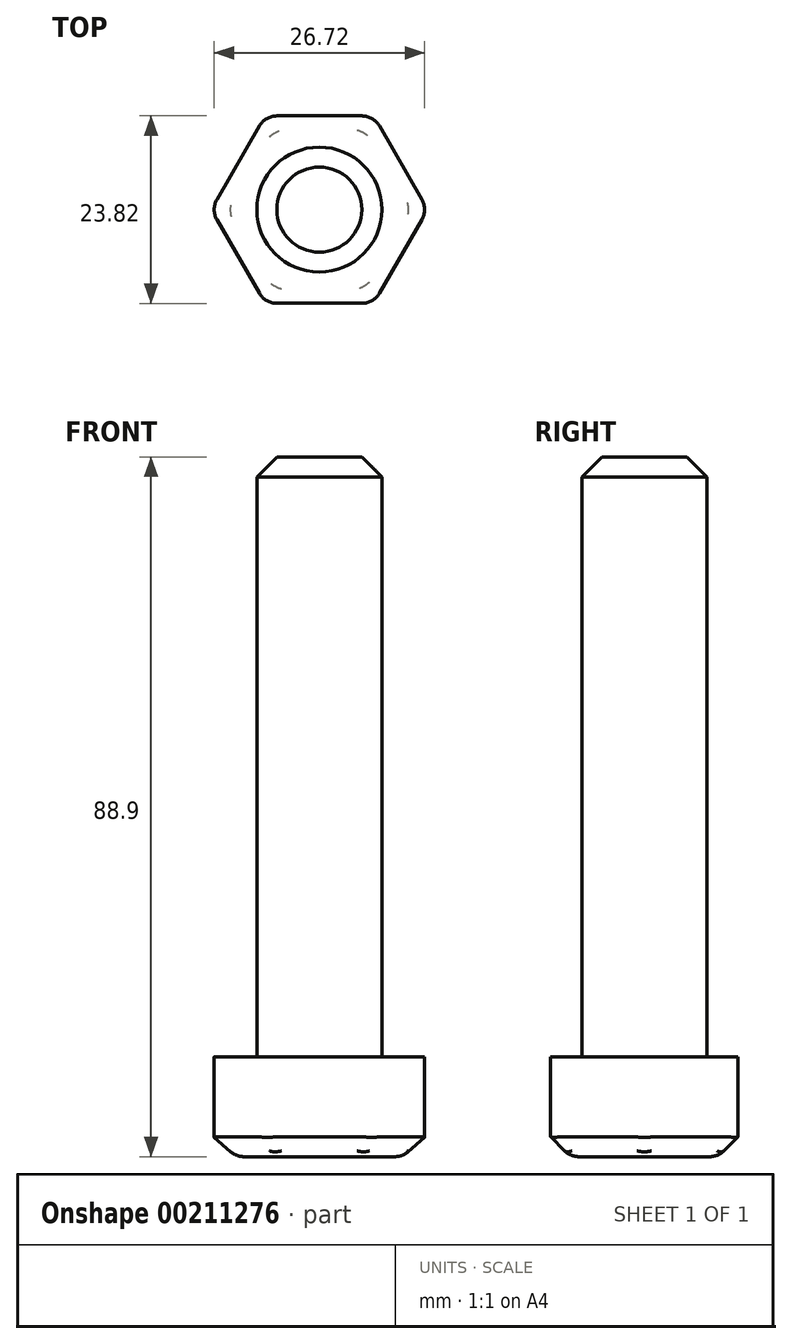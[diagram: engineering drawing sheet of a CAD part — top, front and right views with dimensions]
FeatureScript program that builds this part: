
annotation { "Feature Type Name" : "Feature", "Feature Type Description" : "" }
export const myFeature = defineFeature(function(context is Context, id is Id, definition is map)
    precondition{}
    {
        {
            var Q0;
            Q0=qCreatedBy(makeId("Top.planeOp"),FACE);
            var sketch = newSketch(context, id + "F0", { "sketchPlane" : qUnion([Q0])});
            skCircle(sketch, "E0.cCircle", {"center": v(0, 0) * mm, "radius": 11.9 * mm, "construction": true});
            skLineSegment(sketch, "E0.0", {"start": v(-6.87, 11.9) * mm, "end": v(6.87, 11.9) * mm});
            skLineSegment(sketch, "E0.1", {"start": v(6.87, 11.9) * mm, "end": v(13.75, 0) * mm});
            skLineSegment(sketch, "E0.2", {"start": v(13.75, 0) * mm, "end": v(6.87, -11.9) * mm});
            skLineSegment(sketch, "E0.3", {"start": v(6.87, -11.9) * mm, "end": v(-6.87, -11.9) * mm});
            skLineSegment(sketch, "E0.4", {"start": v(-6.87, -11.9) * mm, "end": v(-13.75, 0) * mm});
            skLineSegment(sketch, "E0.5", {"start": v(-13.75, 0) * mm, "end": v(-6.87, 11.9) * mm});
            skPoint(sketch, "E0.0.midPoint", {"position": v(0, 11.9) * mm});
            skSolve(sketch);
        }
        {
            var Q0;
            Q0=qSketchRegion(id+"F0",true);
            extrude(context, id + "F1", {"entities" : qUnion([Q0]), "depth" : 12.7 * mm});
        }
        {
            var Q0;
            Q0=makeQuery(id+"F1.opExtrude","CAP_FACE",FACE,{"disambiguationData":[OSD([sQuery(id+"F0.wireOp",EDGE,"E0.0"),sQuery(id+"F0.wireOp",EDGE,"E0.1"),sQuery(id+"F0.wireOp",EDGE,"E0.2"),sQuery(id+"F0.wireOp",EDGE,"E0.3"),sQuery(id+"F0.wireOp",EDGE,"E0.4"),sQuery(id+"F0.wireOp",EDGE,"E0.5")])],"isStart":false});
            var sketch = newSketch(context, id + "F2", { "sketchPlane" : qUnion([Q0])});
            skCircle(sketch, "E1", {"center": v(0, 0) * mm, "radius": 7.94 * mm});
            skSolve(sketch);
        }
        {
            var Q0;
            Q0=qSketchRegion(id+"F2",true);
            extrude(context, id + "F3", {"entities" : qUnion([Q0]), "operationType" : NewBodyOperationType.ADD, "depth" : 76.2 * mm});
        }
        {
            var Q0;
            Q0=makeQuery(id+"F3.opExtrude","CAP_EDGE",EDGE,{"disambiguationData":[OSD([sQuery(id+"F2.wireOp",EDGE,"E1")])],"isStart":false});
            var Q1;
            Q1=makeQuery(id+"F1.opExtrude","CAP_EDGE",EDGE,{"disambiguationData":[OSD([sQuery(id+"F0.wireOp",EDGE,"E0.5")])],"isStart":true});
            var Q2;
            Q2=makeQuery(id+"F1.opExtrude","CAP_EDGE",EDGE,{"disambiguationData":[OSD([sQuery(id+"F0.wireOp",EDGE,"E0.0")])],"isStart":true});
            var Q3;
            Q3=makeQuery(id+"F1.opExtrude","CAP_EDGE",EDGE,{"disambiguationData":[OSD([sQuery(id+"F0.wireOp",EDGE,"E0.1")])],"isStart":true});
            var Q4;
            Q4=makeQuery(id+"F1.opExtrude","CAP_EDGE",EDGE,{"disambiguationData":[OSD([sQuery(id+"F0.wireOp",EDGE,"E0.2")])],"isStart":true});
            var Q5;
            Q5=makeQuery(id+"F1.opExtrude","CAP_EDGE",EDGE,{"disambiguationData":[OSD([sQuery(id+"F0.wireOp",EDGE,"E0.3")])],"isStart":true});
            var Q6;
            Q6=makeQuery(id+"F1.opExtrude","CAP_EDGE",EDGE,{"disambiguationData":[OSD([sQuery(id+"F0.wireOp",EDGE,"E0.4")])],"isStart":true});
            chamfer(context, id + "F4", {"entities" : qUnion([Q0, Q1, Q2, Q3, Q4, Q5, Q6]), "width" : 2.54 * mm, "tangentPropagation" : true});
        }
        {
            var Q0;
            Q0=makeQuery(id+"F1.opExtrude","SWEPT_EDGE",EDGE,{"disambiguationData":[OSD([sQuery(id+"F0.wireOp",EDGE,"E0.0"),sQuery(id+"F0.wireOp",EDGE,"E0.5")])]});
            var Q1;
            Q1=makeQuery(id+"F1.opExtrude","SWEPT_EDGE",EDGE,{"disambiguationData":[OSD([sQuery(id+"F0.wireOp",EDGE,"E0.0"),sQuery(id+"F0.wireOp",EDGE,"E0.1")])]});
            var Q2;
            Q2=makeQuery(id+"F1.opExtrude","SWEPT_EDGE",EDGE,{"disambiguationData":[OSD([sQuery(id+"F0.wireOp",EDGE,"E0.1"),sQuery(id+"F0.wireOp",EDGE,"E0.2")])]});
            var Q3;
            Q3=makeQuery(id+"F1.opExtrude","SWEPT_EDGE",EDGE,{"disambiguationData":[OSD([sQuery(id+"F0.wireOp",EDGE,"E0.2"),sQuery(id+"F0.wireOp",EDGE,"E0.3")])]});
            var Q4;
            Q4=makeQuery(id+"F1.opExtrude","SWEPT_EDGE",EDGE,{"disambiguationData":[OSD([sQuery(id+"F0.wireOp",EDGE,"E0.3"),sQuery(id+"F0.wireOp",EDGE,"E0.4")])]});
            var Q5;
            Q5=makeQuery(id+"F1.opExtrude","SWEPT_EDGE",EDGE,{"disambiguationData":[OSD([sQuery(id+"F0.wireOp",EDGE,"E0.4"),sQuery(id+"F0.wireOp",EDGE,"E0.5")])]});
            var Q6;
            Q6=makeQuery(id+"F4.opChamfer","BLEND_EDGE",EDGE,{"blendedFrom":[makeQuery(id+"F1.opExtrude","CAP_EDGE",EDGE,{"disambiguationData":[OSD([sQuery(id+"F0.wireOp",EDGE,"E0.3")])],"isStart":true}),makeQuery(id+"F1.opExtrude","CAP_EDGE",EDGE,{"disambiguationData":[OSD([sQuery(id+"F0.wireOp",EDGE,"E0.4")])],"isStart":true})],"blendedInto":[]});
            var Q7;
            Q7=makeQuery(id+"F4.opChamfer","BLEND_EDGE",EDGE,{"blendedFrom":[makeQuery(id+"F1.opExtrude","CAP_EDGE",EDGE,{"disambiguationData":[OSD([sQuery(id+"F0.wireOp",EDGE,"E0.2")])],"isStart":true}),makeQuery(id+"F1.opExtrude","CAP_EDGE",EDGE,{"disambiguationData":[OSD([sQuery(id+"F0.wireOp",EDGE,"E0.3")])],"isStart":true})],"blendedInto":[]});
            var Q8;
            Q8=makeQuery(id+"F4.opChamfer","BLEND_EDGE",EDGE,{"blendedFrom":[makeQuery(id+"F1.opExtrude","CAP_EDGE",EDGE,{"disambiguationData":[OSD([sQuery(id+"F0.wireOp",EDGE,"E0.1")])],"isStart":true}),makeQuery(id+"F1.opExtrude","CAP_EDGE",EDGE,{"disambiguationData":[OSD([sQuery(id+"F0.wireOp",EDGE,"E0.2")])],"isStart":true})],"blendedInto":[]});
            var Q9;
            Q9=makeQuery(id+"F4.opChamfer","BLEND_EDGE",EDGE,{"blendedFrom":[makeQuery(id+"F1.opExtrude","CAP_EDGE",EDGE,{"disambiguationData":[OSD([sQuery(id+"F0.wireOp",EDGE,"E0.0")])],"isStart":true}),makeQuery(id+"F1.opExtrude","CAP_EDGE",EDGE,{"disambiguationData":[OSD([sQuery(id+"F0.wireOp",EDGE,"E0.1")])],"isStart":true})],"blendedInto":[]});
            var Q10;
            Q10=makeQuery(id+"F4.opChamfer","BLEND_EDGE",EDGE,{"blendedFrom":[makeQuery(id+"F1.opExtrude","CAP_EDGE",EDGE,{"disambiguationData":[OSD([sQuery(id+"F0.wireOp",EDGE,"E0.0")])],"isStart":true}),makeQuery(id+"F1.opExtrude","CAP_EDGE",EDGE,{"disambiguationData":[OSD([sQuery(id+"F0.wireOp",EDGE,"E0.5")])],"isStart":true})],"blendedInto":[]});
            var Q11;
            Q11=makeQuery(id+"F4.opChamfer","BLEND_EDGE",EDGE,{"blendedFrom":[makeQuery(id+"F1.opExtrude","CAP_EDGE",EDGE,{"disambiguationData":[OSD([sQuery(id+"F0.wireOp",EDGE,"E0.4")])],"isStart":true}),makeQuery(id+"F1.opExtrude","CAP_EDGE",EDGE,{"disambiguationData":[OSD([sQuery(id+"F0.wireOp",EDGE,"E0.5")])],"isStart":true})],"blendedInto":[]});
            var Q12;
            {var subQ0=sQuery(id+"F0.wireOp",EDGE,"E0.4");Q12=makeQuery(id+"F4.opChamfer","BLEND_EDGE",EDGE,{"blendedFrom":[makeQuery(id+"F1.opExtrude","CAP_EDGE",EDGE,{"disambiguationData":[OSD([subQ0])],"isStart":true}),makeQuery(id+"F1.opExtrude","CAP_FACE",FACE,{"disambiguationData":[OSD([sQuery(id+"F0.wireOp",EDGE,"E0.0"),sQuery(id+"F0.wireOp",EDGE,"E0.1"),sQuery(id+"F0.wireOp",EDGE,"E0.2"),sQuery(id+"F0.wireOp",EDGE,"E0.3"),subQ0,sQuery(id+"F0.wireOp",EDGE,"E0.5")])],"isStart":true})],"blendedInto":[makeQuery(id+"F1.opExtrude","CAP_FACE",FACE,{"disambiguationData":[OSD([sQuery(id+"F0.wireOp",EDGE,"E0.0"),sQuery(id+"F0.wireOp",EDGE,"E0.1"),sQuery(id+"F0.wireOp",EDGE,"E0.2"),sQuery(id+"F0.wireOp",EDGE,"E0.3"),subQ0,sQuery(id+"F0.wireOp",EDGE,"E0.5")])],"isStart":true})]});}
            var Q13;
            {var subQ0=sQuery(id+"F0.wireOp",EDGE,"E0.3");Q13=makeQuery(id+"F4.opChamfer","BLEND_EDGE",EDGE,{"blendedFrom":[makeQuery(id+"F1.opExtrude","CAP_EDGE",EDGE,{"disambiguationData":[OSD([subQ0])],"isStart":true}),makeQuery(id+"F1.opExtrude","CAP_FACE",FACE,{"disambiguationData":[OSD([sQuery(id+"F0.wireOp",EDGE,"E0.0"),sQuery(id+"F0.wireOp",EDGE,"E0.1"),sQuery(id+"F0.wireOp",EDGE,"E0.2"),subQ0,sQuery(id+"F0.wireOp",EDGE,"E0.4"),sQuery(id+"F0.wireOp",EDGE,"E0.5")])],"isStart":true})],"blendedInto":[makeQuery(id+"F1.opExtrude","CAP_FACE",FACE,{"disambiguationData":[OSD([sQuery(id+"F0.wireOp",EDGE,"E0.0"),sQuery(id+"F0.wireOp",EDGE,"E0.1"),sQuery(id+"F0.wireOp",EDGE,"E0.2"),subQ0,sQuery(id+"F0.wireOp",EDGE,"E0.4"),sQuery(id+"F0.wireOp",EDGE,"E0.5")])],"isStart":true})]});}
            var Q14;
            {var subQ0=sQuery(id+"F0.wireOp",EDGE,"E0.2");Q14=makeQuery(id+"F4.opChamfer","BLEND_EDGE",EDGE,{"blendedFrom":[makeQuery(id+"F1.opExtrude","CAP_EDGE",EDGE,{"disambiguationData":[OSD([subQ0])],"isStart":true}),makeQuery(id+"F1.opExtrude","CAP_FACE",FACE,{"disambiguationData":[OSD([sQuery(id+"F0.wireOp",EDGE,"E0.0"),sQuery(id+"F0.wireOp",EDGE,"E0.1"),subQ0,sQuery(id+"F0.wireOp",EDGE,"E0.3"),sQuery(id+"F0.wireOp",EDGE,"E0.4"),sQuery(id+"F0.wireOp",EDGE,"E0.5")])],"isStart":true})],"blendedInto":[makeQuery(id+"F1.opExtrude","CAP_FACE",FACE,{"disambiguationData":[OSD([sQuery(id+"F0.wireOp",EDGE,"E0.0"),sQuery(id+"F0.wireOp",EDGE,"E0.1"),subQ0,sQuery(id+"F0.wireOp",EDGE,"E0.3"),sQuery(id+"F0.wireOp",EDGE,"E0.4"),sQuery(id+"F0.wireOp",EDGE,"E0.5")])],"isStart":true})]});}
            var Q15;
            {var subQ0=sQuery(id+"F0.wireOp",EDGE,"E0.1");Q15=makeQuery(id+"F4.opChamfer","BLEND_EDGE",EDGE,{"blendedFrom":[makeQuery(id+"F1.opExtrude","CAP_EDGE",EDGE,{"disambiguationData":[OSD([subQ0])],"isStart":true}),makeQuery(id+"F1.opExtrude","CAP_FACE",FACE,{"disambiguationData":[OSD([sQuery(id+"F0.wireOp",EDGE,"E0.0"),subQ0,sQuery(id+"F0.wireOp",EDGE,"E0.2"),sQuery(id+"F0.wireOp",EDGE,"E0.3"),sQuery(id+"F0.wireOp",EDGE,"E0.4"),sQuery(id+"F0.wireOp",EDGE,"E0.5")])],"isStart":true})],"blendedInto":[makeQuery(id+"F1.opExtrude","CAP_FACE",FACE,{"disambiguationData":[OSD([sQuery(id+"F0.wireOp",EDGE,"E0.0"),subQ0,sQuery(id+"F0.wireOp",EDGE,"E0.2"),sQuery(id+"F0.wireOp",EDGE,"E0.3"),sQuery(id+"F0.wireOp",EDGE,"E0.4"),sQuery(id+"F0.wireOp",EDGE,"E0.5")])],"isStart":true})]});}
            var Q16;
            {var subQ0=sQuery(id+"F0.wireOp",EDGE,"E0.0");Q16=makeQuery(id+"F4.opChamfer","BLEND_EDGE",EDGE,{"blendedFrom":[makeQuery(id+"F1.opExtrude","CAP_EDGE",EDGE,{"disambiguationData":[OSD([subQ0])],"isStart":true}),makeQuery(id+"F1.opExtrude","CAP_FACE",FACE,{"disambiguationData":[OSD([subQ0,sQuery(id+"F0.wireOp",EDGE,"E0.1"),sQuery(id+"F0.wireOp",EDGE,"E0.2"),sQuery(id+"F0.wireOp",EDGE,"E0.3"),sQuery(id+"F0.wireOp",EDGE,"E0.4"),sQuery(id+"F0.wireOp",EDGE,"E0.5")])],"isStart":true})],"blendedInto":[makeQuery(id+"F1.opExtrude","CAP_FACE",FACE,{"disambiguationData":[OSD([subQ0,sQuery(id+"F0.wireOp",EDGE,"E0.1"),sQuery(id+"F0.wireOp",EDGE,"E0.2"),sQuery(id+"F0.wireOp",EDGE,"E0.3"),sQuery(id+"F0.wireOp",EDGE,"E0.4"),sQuery(id+"F0.wireOp",EDGE,"E0.5")])],"isStart":true})]});}
            var Q17;
            {var subQ0=sQuery(id+"F0.wireOp",EDGE,"E0.5");Q17=makeQuery(id+"F4.opChamfer","BLEND_EDGE",EDGE,{"blendedFrom":[makeQuery(id+"F1.opExtrude","CAP_EDGE",EDGE,{"disambiguationData":[OSD([subQ0])],"isStart":true}),makeQuery(id+"F1.opExtrude","CAP_FACE",FACE,{"disambiguationData":[OSD([sQuery(id+"F0.wireOp",EDGE,"E0.0"),sQuery(id+"F0.wireOp",EDGE,"E0.1"),sQuery(id+"F0.wireOp",EDGE,"E0.2"),sQuery(id+"F0.wireOp",EDGE,"E0.3"),sQuery(id+"F0.wireOp",EDGE,"E0.4"),subQ0])],"isStart":true})],"blendedInto":[makeQuery(id+"F1.opExtrude","CAP_FACE",FACE,{"disambiguationData":[OSD([sQuery(id+"F0.wireOp",EDGE,"E0.0"),sQuery(id+"F0.wireOp",EDGE,"E0.1"),sQuery(id+"F0.wireOp",EDGE,"E0.2"),sQuery(id+"F0.wireOp",EDGE,"E0.3"),sQuery(id+"F0.wireOp",EDGE,"E0.4"),subQ0])],"isStart":true})]});}
            fillet(context, id + "F5", {"entities" : qUnion([Q0, Q1, Q2, Q3, Q4, Q5, Q6, Q7, Q8, Q9, Q10, Q11, Q12, Q13, Q14, Q15, Q16, Q17]), "radius" : 2.54 * mm, "tangentPropagation" : true, "allowEdgeOverflow" : false});
        }
    });
